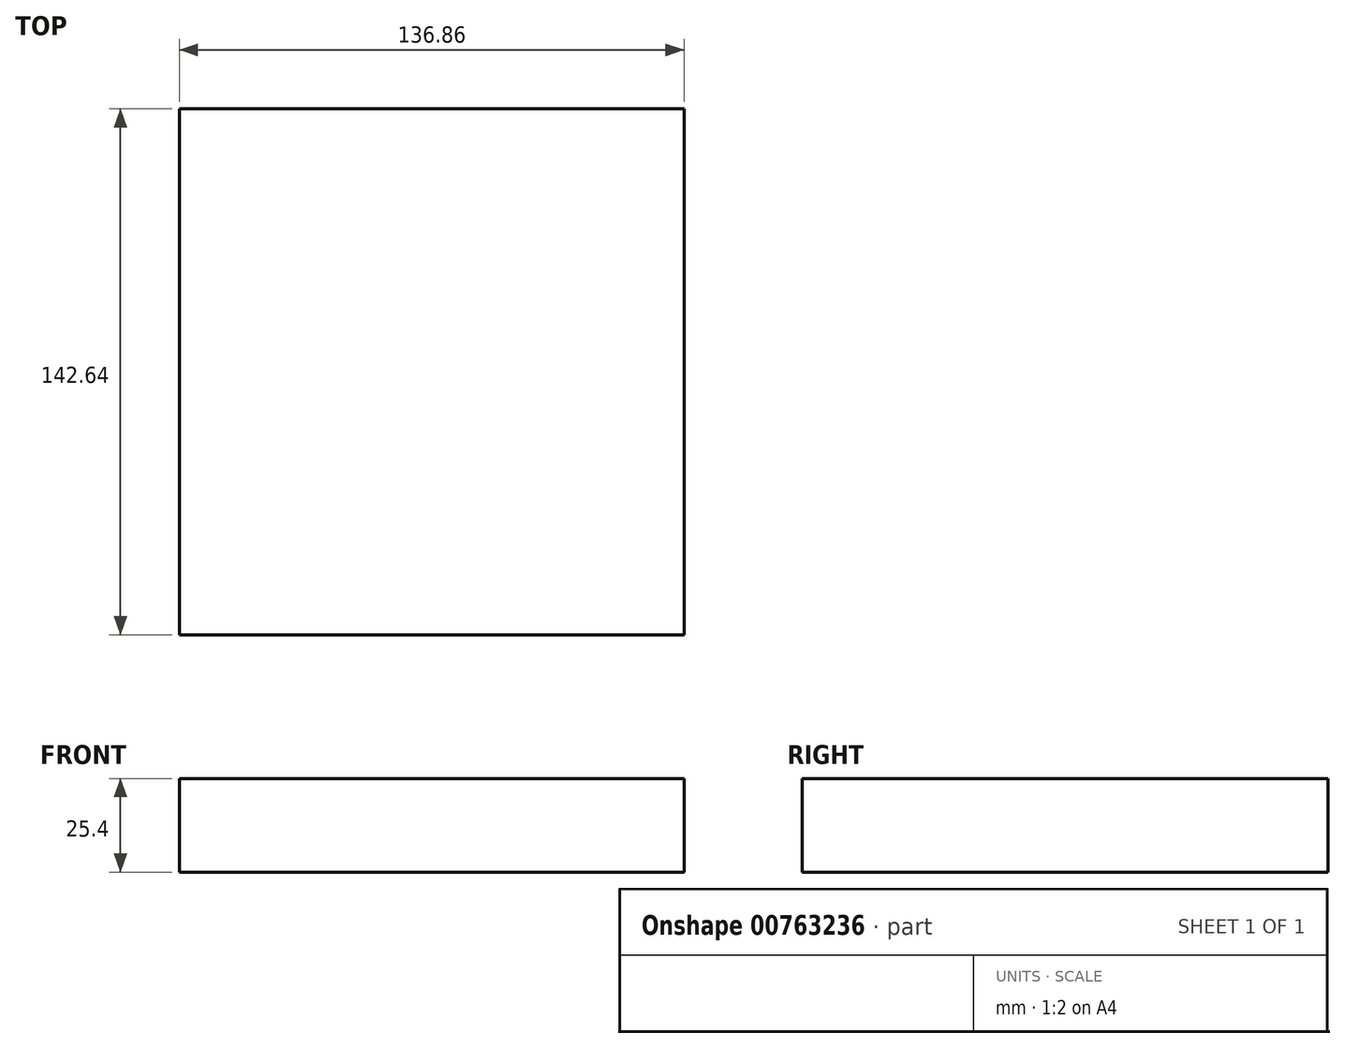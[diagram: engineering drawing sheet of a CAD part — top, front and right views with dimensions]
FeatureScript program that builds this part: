
annotation { "Feature Type Name" : "Feature", "Feature Type Description" : "" }
export const myFeature = defineFeature(function(context is Context, id is Id, definition is map)
    precondition{}
    {
        {
            var Q0;
            Q0=qCreatedBy(makeId("Top.planeOp"),FACE);
            var sketch = newSketch(context, id + "F0", { "sketchPlane" : qUnion([Q0])});
            skLineSegment(sketch, "E0.bottom", {"start": v(-68.43, 68.88) * mm, "end": v(68.43, 68.88) * mm});
            skLineSegment(sketch, "E0.top", {"start": v(-68.43, -73.76) * mm, "end": v(68.43, -73.76) * mm});
            skLineSegment(sketch, "E0.left", {"start": v(-68.43, 68.88) * mm, "end": v(-68.43, -73.76) * mm});
            skLineSegment(sketch, "E0.right", {"start": v(68.43, 68.88) * mm, "end": v(68.43, -73.76) * mm});
            skPoint(sketch, "E0.middle", {"position": v(0, -2.44) * mm});
            skSolve(sketch);
        }
        {
            var Q0;
            Q0=makeQuery(id+"F0.imprint","IMPRINT",FACE,{"disambiguationData":[TD([[makeQuery(id+"F0.imprint","IMPRINT",EDGE,{"derivedFrom":sQuery(id+"F0.wireOp",EDGE,"E0.bottom")}),-1.0]])]});
            extrude(context, id + "F1", {"entities" : qUnion([Q0]), "depth" : 25.4 * mm, "offsetDistance" : 25.4 * mm});
        }
        {
            var Q0;
            Q0=qCreatedBy(makeId("Top.planeOp"),FACE);
            cPlane(context, id + "F2", {"entities" : qUnion([Q0]), "cplaneType" : CPlaneType.OFFSET, "offset" : 25.4 * mm, "width" : 152.4 * mm, "height" : 152.4 * mm});
        }
    });
